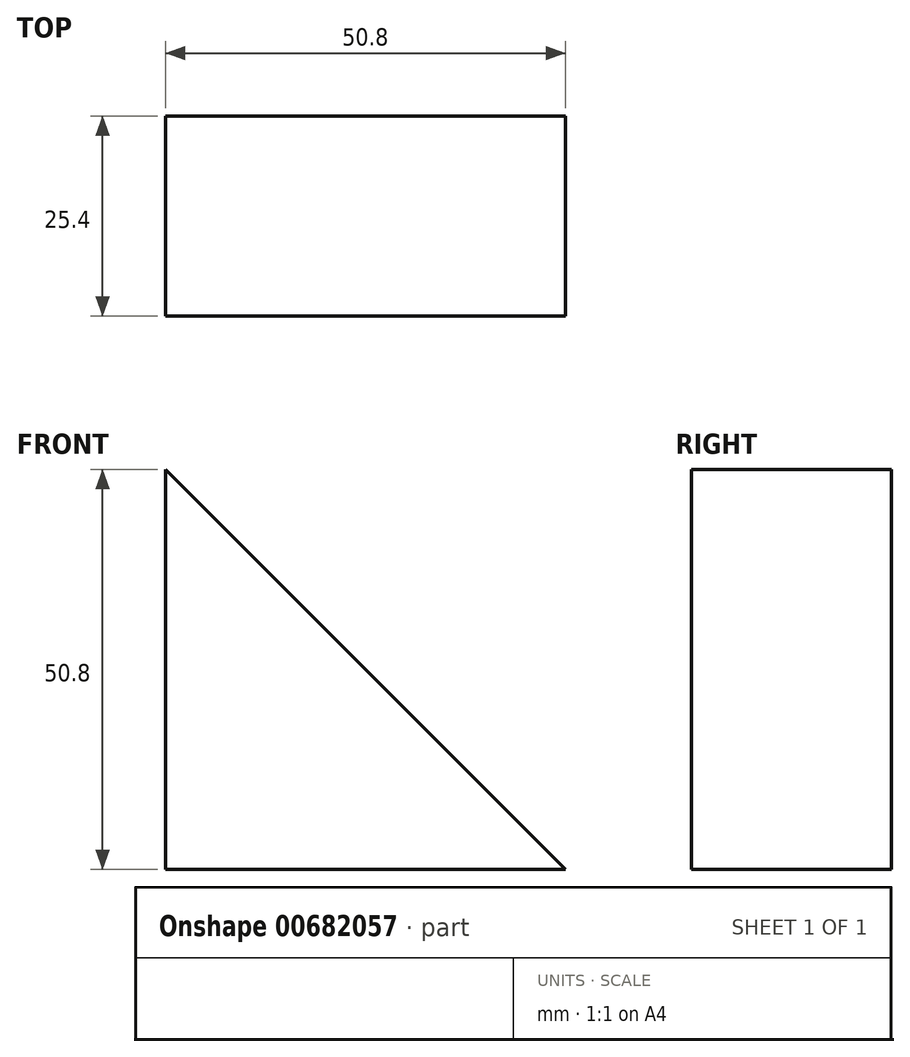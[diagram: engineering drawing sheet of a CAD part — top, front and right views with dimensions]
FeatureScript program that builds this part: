
annotation { "Feature Type Name" : "Feature", "Feature Type Description" : "" }
export const myFeature = defineFeature(function(context is Context, id is Id, definition is map)
    precondition{}
    {
        {
            var Q0;
            Q0=qCreatedBy(makeId("Front.planeOp"),FACE);
            var sketch = newSketch(context, id + "F0", { "sketchPlane" : qUnion([Q0])});
            skLineSegment(sketch, "E0", {"start": v(-29.7, 25.12) * mm, "end": v(-29.7, -25.68) * mm});
            skLineSegment(sketch, "E1", {"start": v(-29.7, -25.68) * mm, "end": v(21.1, -25.68) * mm});
            skLineSegment(sketch, "E2", {"start": v(-29.7, 25.12) * mm, "end": v(21.1, -25.68) * mm});
            skSolve(sketch);
        }
        {
            var Q0;
            Q0 = qSketchRegion(id + "F0", true);
            extrude(context, id + "F1", {"entities" : qUnion([Q0]), "depth" : 25.4 * mm, "offsetDistance" : 25.4 * mm});
        }
    });
